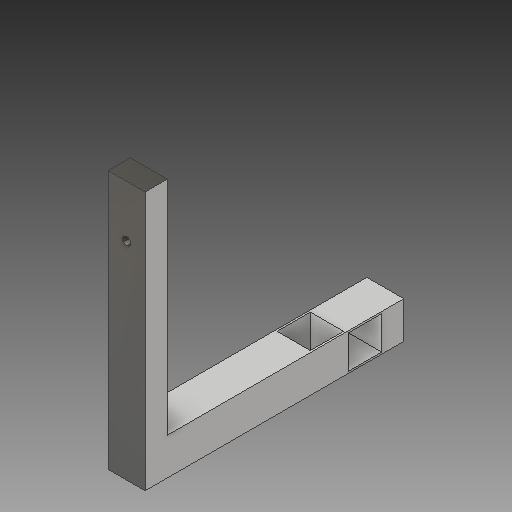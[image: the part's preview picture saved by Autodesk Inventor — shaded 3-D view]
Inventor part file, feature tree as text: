
AUTODESK INVENTOR PART (.ipt)
format: ipt  version: 2019 (Build 230136000, 136)  size: 157,696 bytes
history: native  units: mm
features: sketch x7, extrude x4, hole x3
ambient origin geometry x8: Origin, YZ Plane, XZ Plane, XY Plane, X Axis, Y Axis, Z Axis, Center Point
bodies: Solid1 (feature_tree)
feature tree (14):
  extrude  "Extrusion1"  Depth=50.0mm
  extrude  "Extrusion2"  Depth=25.0mm
  hole  "Hole1"  [1 undecoded]
  extrude  "Extrusion3"  Depth=300.0mm
  hole  "Hole4"  [1 undecoded]
  extrude  "Extrusion4"  Depth=30.0mm
  hole  "Hole5"  [1 undecoded]
  sketch  "Sketch1"  dims[d0=50.0mm d1=25.0mm]
  sketch  "Sketch2"  dims[d2=25.0mm d3=25.0mm]
  sketch  "Sketch3"  dims[d4=350.0mm d5=0.0mm d6=30.0mm]
  sketch  "Sketch6"  dims[d7=300.0mm d8=0.0mm d9=70.0mm]
  sketch  "Sketch7"  dims[d10=25.0mm]
  sketch  "Sketch8"  dims[d11=10.917mm d12=24.0mm d13=4.0mm d14=2.0mm d15=90.0deg d16=29.1mm d17=20.594885mm d36=45.0mm]
  sketch  "Sketch9"  dims[d37=45.0mm d38=30.0mm d39=2.5mm d40=50.0mm d41=0.0mm d42=102.0mm d43=25.0mm d44=11.835mm d45=28.0mm d46=4.0mm d47=2.0mm d48=90.0deg d49=37.3mm d50=20.594885mm d51=45.0mm d52=45.0mm d53=79.0mm d54=2.5mm d55=50.0mm d56=0.0mm d57=52.5mm d58=25.0mm d59=11.835mm d60=28.0mm d61=4.0mm d62=2.0mm d63=90.0deg d64=41.3mm d65=20.594885mm]
note: 3 required parameter values undecoded (feature->parameter linkage not recoverable at this tier; creation-order binding heuristic only, values carry confidence <= 0.55)
